# Revit family: Elsa Beam 2 Seater
name_source: partatom
category: Furniture
revit_build: Autodesk Revit 2016 (Build: 20160525_1230(x64)
units: mm (PartAtom-declared; Revit-internal decimal feet)

## family parameters
Always vertical = Yes
Cut with Voids When Loaded = No
OmniClass Number = 23.40.00.00
OmniClass Title = Equipment and Furnishings
Room Calculation Point = No
Shared = No
Work Plane-Based = No

## types (4) — shared parameters
Assembly Code = E2020200
Back = Gresham - Grey Fabric
Bung = Gresham - Black Plastic
Foot = Gresham - Grey Fabric
Frame = Gresham - Chrome
Manufacturer = Gresham Office Funiture
Model = ELSA BEAM
Range = SEATING
Seat = Gresham - Grey Fabric
Seat 2 (Hidden) = Yes
Table = No
URL = www.gof.co.uk

## per-type parameters (varying)
| type | Angled End Frame | Arms | Arms 2 (Hidden) | No Arms | No Arms (Hidden) | Product Code | Triangular End Frame |
| Triangular End Frame no Arms | No | No | No | Yes | Yes | EQR2 (No Arms) | Yes |
| Triangular End Frame with Arms | No | Yes | Yes | No | No | EQR2 (With Arms) | Yes |
| Angled End Frame with Arms | Yes | Yes | Yes | No | No | EQA2 (With Arms) | No |
| Angled End Frame no Arms | Yes | No | No | Yes | Yes | EQA2 (No Arms) | No |

## geometry (parser evidence)
native form markers: Sweep x19
no freeform markers — native parametric forms only
